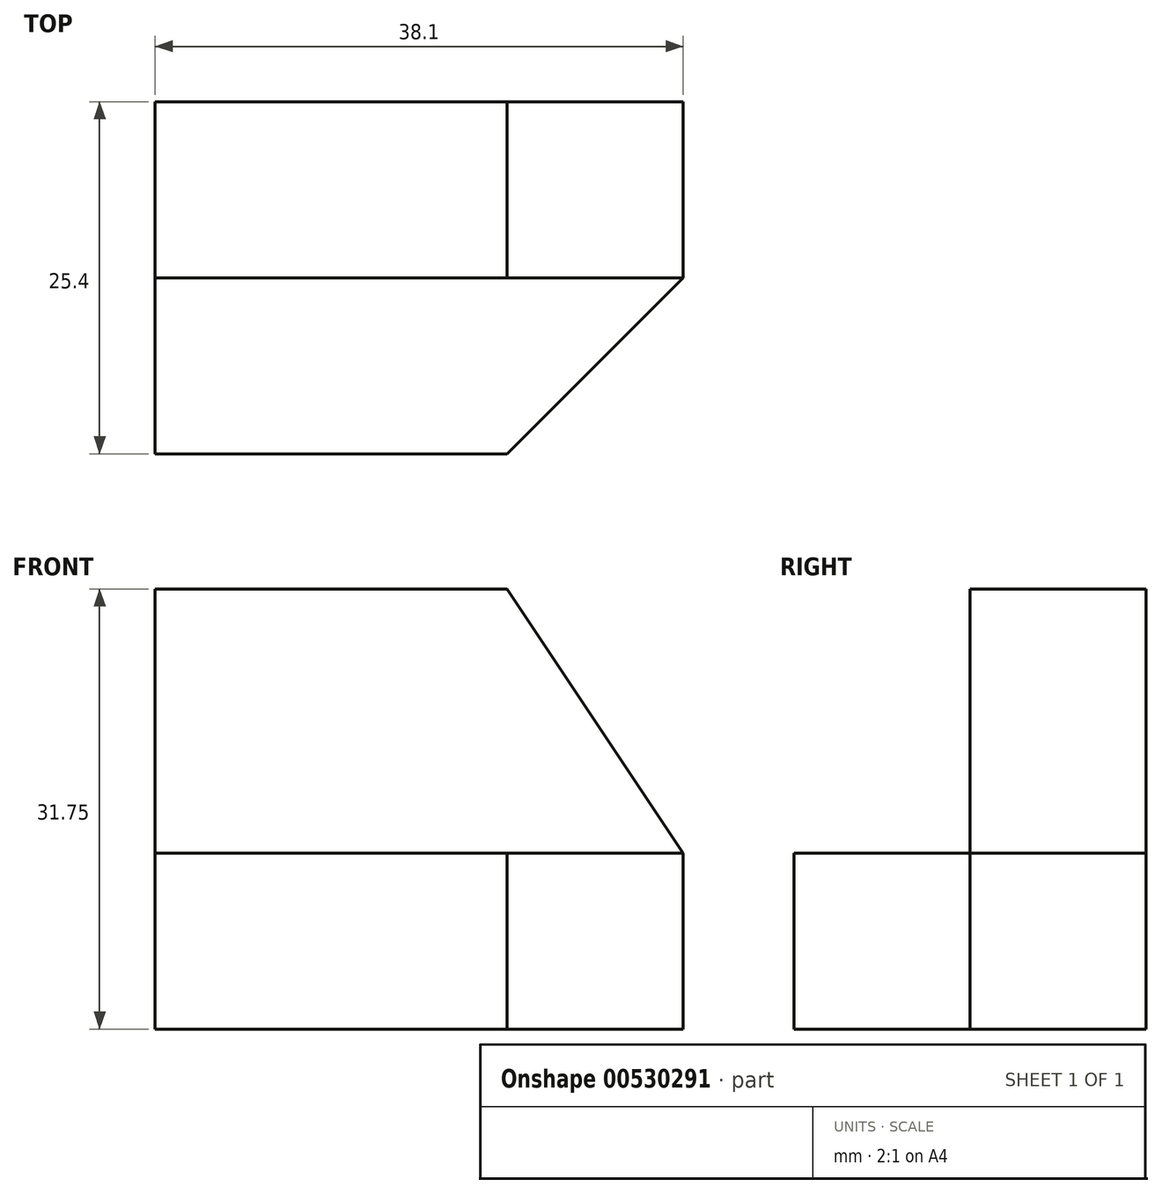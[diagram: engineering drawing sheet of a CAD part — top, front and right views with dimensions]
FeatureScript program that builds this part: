
annotation { "Feature Type Name" : "Feature", "Feature Type Description" : "" }
export const myFeature = defineFeature(function(context is Context, id is Id, definition is map)
    precondition{}
    {
        {
            var Q0;
            Q0=qCreatedBy(makeId("Right.planeOp"),FACE);
            var sketch = newSketch(context, id + "F0", { "sketchPlane" : qUnion([Q0])});
            skLineSegment(sketch, "E0", {"start": v(12.7, 31.75) * mm, "end": v(12.7, 0) * mm});
            skLineSegment(sketch, "E1", {"start": v(12.7, 0) * mm, "end": v(-12.7, 0) * mm});
            skLineSegment(sketch, "E2", {"start": v(-12.7, 0) * mm, "end": v(-12.7, 12.7) * mm});
            skLineSegment(sketch, "E3", {"start": v(-12.7, 12.7) * mm, "end": v(0, 12.7) * mm});
            skLineSegment(sketch, "E4", {"start": v(0, 12.7) * mm, "end": v(0, 31.75) * mm});
            skLineSegment(sketch, "E5", {"start": v(12.7, 31.75) * mm, "end": v(0, 31.75) * mm});
            skSolve(sketch);
        }
        {
            var Q0;
            Q0=makeQuery(id+"F0.imprint","IMPRINT",FACE,{"disambiguationData":[TD([[makeQuery(id+"F0.imprint","IMPRINT",EDGE,{"derivedFrom":sQuery(id+"F0.wireOp",EDGE,"E0")}),-1.0]])]});
            extrude(context, id + "F1", {"entities" : qUnion([Q0]), "depth" : 38.1 * mm, "offsetDistance" : 25.4 * mm});
        }
        {
            var Q0;
            Q0=makeQuery(id+"F1.opExtrude","SWEPT_FACE",FACE,{"disambiguationData":[OSD([sQuery(id+"F0.wireOp",EDGE,"E4")])]});
            var sketch = newSketch(context, id + "F2", { "sketchPlane" : qUnion([Q0])});
            skLineSegment(sketch, "E6", {"start": v(25.4, 31.75) * mm, "end": v(38.1, 12.7) * mm});
            skSolve(sketch);
        }
        {
            var Q0;
            {var subQ0=sQuery(id+"F2.wireOp",EDGE,"E6");Q0=makeQuery(id+"F2.imprint","IMPRINT",FACE,{"disambiguationData":[TD([[makeQuery(id+"F2.imprint","IMPRINT",EDGE,{"derivedFrom":subQ0}),1.0]])]});}
            extrude(context, id + "F3", {"entities" : qUnion([Q0]), "operationType" : NewBodyOperationType.REMOVE, "oppositeDirection" : true, "depth" : 12.7 * mm, "offsetDistance" : 25.4 * mm});
        }
        {
            var Q0;
            Q0=makeQuery(id+"F1.opExtrude","SWEPT_FACE",FACE,{"disambiguationData":[OSD([sQuery(id+"F0.wireOp",EDGE,"E3")])]});
            var sketch = newSketch(context, id + "F4", { "sketchPlane" : qUnion([Q0])});
            skLineSegment(sketch, "E7", {"start": v(38.1, 0) * mm, "end": v(25.4, -12.7) * mm});
            skSolve(sketch);
        }
        {
            var Q0;
            {var subQ0=sQuery(id+"F4.wireOp",EDGE,"E7");Q0=makeQuery(id+"F4.imprint","IMPRINT",FACE,{"disambiguationData":[TD([[makeQuery(id+"F4.imprint","IMPRINT",EDGE,{"derivedFrom":subQ0}),1.0]])]});}
            extrude(context, id + "F5", {"entities" : qUnion([Q0]), "operationType" : NewBodyOperationType.REMOVE, "oppositeDirection" : true, "depth" : 12.7 * mm, "offsetDistance" : 25.4 * mm});
        }
    });
